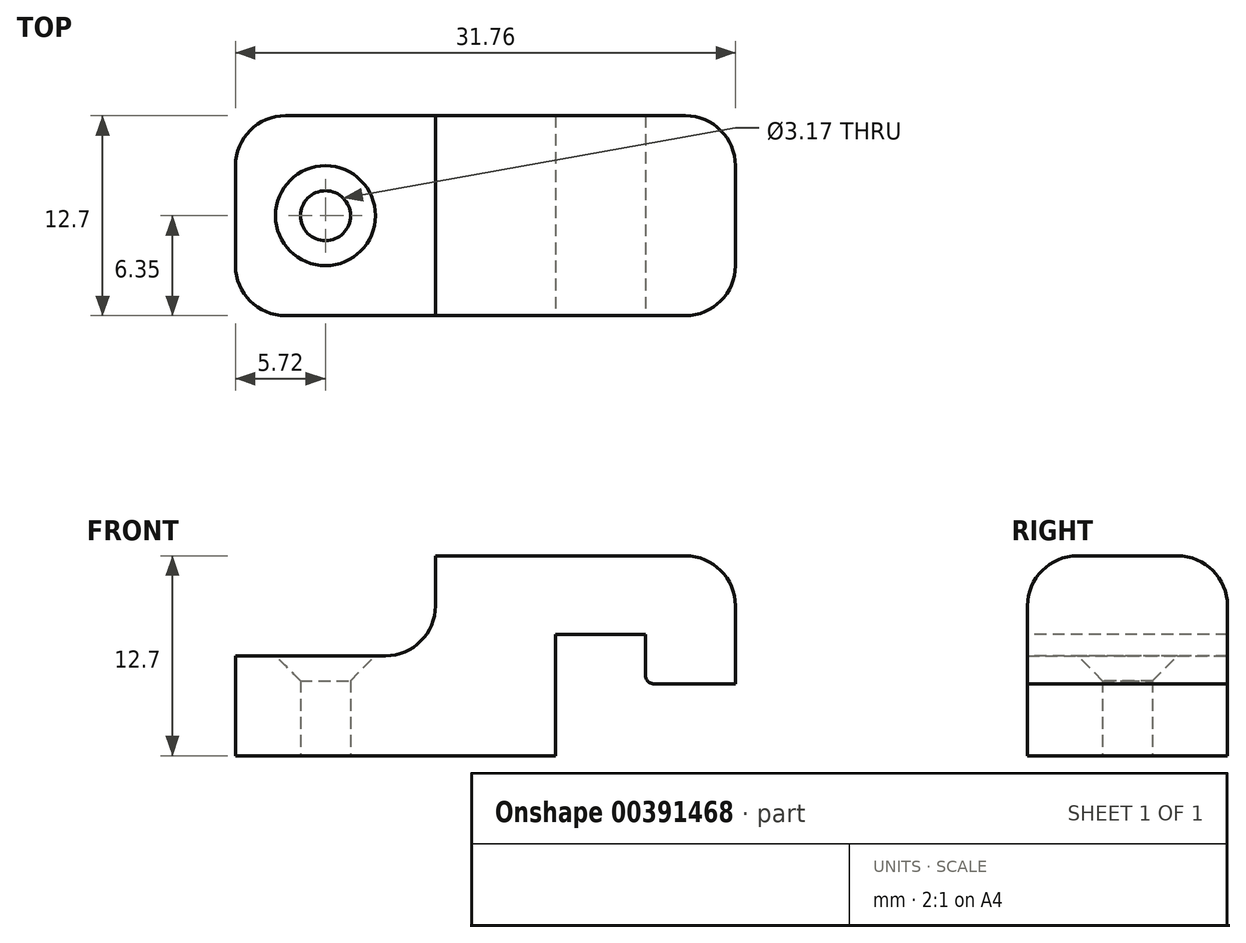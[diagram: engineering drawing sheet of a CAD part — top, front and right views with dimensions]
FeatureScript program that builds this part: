
annotation { "Feature Type Name" : "Feature", "Feature Type Description" : "" }
export const myFeature = defineFeature(function(context is Context, id is Id, definition is map)
    precondition{}
    {
        {
            var Q0;
            Q0=qCreatedBy(makeId("Top.planeOp"),FACE);
            var sketch = newSketch(context, id + "F0", { "sketchPlane" : qUnion([Q0])});
            skLineSegment(sketch, "E0.bottom", {"start": v(15.88, 6.35) * mm, "end": v(-15.88, 6.35) * mm});
            skLineSegment(sketch, "E0.top", {"start": v(15.88, -6.35) * mm, "end": v(-15.88, -6.35) * mm});
            skLineSegment(sketch, "E0.left", {"start": v(15.88, 6.35) * mm, "end": v(15.88, -6.35) * mm});
            skLineSegment(sketch, "E0.right", {"start": v(-15.88, 6.35) * mm, "end": v(-15.88, -6.35) * mm});
            skPoint(sketch, "E0.middle", {"position": v(0, 0) * mm});
            skCircle(sketch, "E1", {"center": v(-10.16, 0) * mm, "radius": 1.59 * mm});
            skSolve(sketch);
        }
        {
            var Q0;
            Q0 = qSketchRegion(id + "F0", true);
            extrude(context, id + "F1", {"entities" : qUnion([Q0]), "depth" : 12.7 * mm});
        }
        {
            var Q0;
            Q0=makeQuery(id+"F1.opExtrude","SWEPT_FACE",FACE,{"disambiguationData":[OSD([sQuery(id+"F0.wireOp",EDGE,"E0.top")])]});
            var sketch = newSketch(context, id + "F2", { "sketchPlane" : qUnion([Q0])});
            skLineSegment(sketch, "E2.bottom", {"start": v(15.88, 0) * mm, "end": v(4.44, 0) * mm});
            skLineSegment(sketch, "E2.top", {"start": v(15.88, 4.57) * mm, "end": v(10.7, 4.57) * mm});
            skLineSegment(sketch, "E2.left", {"start": v(15.88, 0) * mm, "end": v(15.88, 4.57) * mm});
            skLineSegment(sketch, "E2.right", {"start": v(4.44, 0) * mm, "end": v(4.44, 4.57) * mm});
            skLineSegment(sketch, "E3.top", {"start": v(4.44, 7.7) * mm, "end": v(10.16, 7.7) * mm});
            skLineSegment(sketch, "E3.left", {"start": v(4.44, 4.57) * mm, "end": v(4.44, 7.7) * mm});
            skLineSegment(sketch, "E3.right", {"start": v(10.16, 5.1) * mm, "end": v(10.16, 7.7) * mm});
            skPoint(sketch, "E4.visualSharp", {"position": v(10.16, 4.57) * mm});
            skArc(sketch, "E4.filletArc", {"start": v(10.16, 5.1) * mm, "mid": v(10.32, 4.73) * mm, "end": v(10.7, 4.57) * mm});
            skLineSegment(sketch, "E5.bottom", {"start": v(-15.88, 12.7) * mm, "end": v(-3.17, 12.7) * mm});
            skLineSegment(sketch, "E5.top", {"start": v(-15.88, 6.35) * mm, "end": v(-3.17, 6.35) * mm});
            skLineSegment(sketch, "E5.left", {"start": v(-15.88, 12.7) * mm, "end": v(-15.88, 6.35) * mm});
            skLineSegment(sketch, "E5.right", {"start": v(-3.17, 12.7) * mm, "end": v(-3.17, 6.35) * mm});
            skSolve(sketch);
        }
        {
            var Q0;
            Q0=makeQuery(id+"F1.opExtrude","CAP_EDGE",EDGE,{"disambiguationData":[OSD([sQuery(id+"F0.wireOp",EDGE,"E0.left")])],"isStart":false});
            var Q1;
            Q1=makeQuery(id+"F1.opExtrude","CAP_EDGE",EDGE,{"disambiguationData":[OSD([sQuery(id+"F0.wireOp",EDGE,"E0.top")])],"isStart":false});
            var Q2;
            Q2=makeQuery(id+"F1.opExtrude","CAP_EDGE",EDGE,{"disambiguationData":[OSD([sQuery(id+"F0.wireOp",EDGE,"E0.bottom")])],"isStart":false});
            var Q3;
            Q3=makeQuery(id+"F1.opExtrude","CAP_EDGE",EDGE,{"disambiguationData":[OSD([sQuery(id+"F0.wireOp",EDGE,"E0.right")])],"isStart":false});
            var Q4;
            Q4=makeQuery(id+"F1.opExtrude","SWEPT_EDGE",EDGE,{"disambiguationData":[OSD([sQuery(id+"F0.wireOp",EDGE,"E0.top"),sQuery(id+"F0.wireOp",EDGE,"E0.right")])]});
            var Q5;
            Q5=makeQuery(id+"F1.opExtrude","SWEPT_EDGE",EDGE,{"disambiguationData":[OSD([sQuery(id+"F0.wireOp",EDGE,"E0.top"),sQuery(id+"F0.wireOp",EDGE,"E0.left")])]});
            var Q6;
            Q6=makeQuery(id+"F1.opExtrude","SWEPT_EDGE",EDGE,{"disambiguationData":[OSD([sQuery(id+"F0.wireOp",EDGE,"E0.bottom"),sQuery(id+"F0.wireOp",EDGE,"E0.right")])]});
            var Q7;
            Q7=makeQuery(id+"F1.opExtrude","SWEPT_EDGE",EDGE,{"disambiguationData":[OSD([sQuery(id+"F0.wireOp",EDGE,"E0.bottom"),sQuery(id+"F0.wireOp",EDGE,"E0.left")])]});
            fillet(context, id + "F3", {"entities" : qUnion([Q0, Q1, Q2, Q3, Q4, Q5, Q6, Q7]), "radius" : 3.17 * mm, "tangentPropagation" : true, "allowEdgeOverflow" : false});
        }
        {
            var Q0;
            Q0 = qSketchRegion(id + "F2", true);
            extrude(context, id + "F4", {"entities" : qUnion([Q0]), "operationType" : NewBodyOperationType.REMOVE, "oppositeDirection" : true, "depth" : 12.7 * mm});
        }
        {
            var Q0;
            Q0=makeQuery(id+"F4.boolean.opBoolean","COPY",EDGE,{"derivedFrom":makeQuery(id+"F4.opExtrude","SWEPT_EDGE",EDGE,{"disambiguationData":[OSD([sQuery(id+"F0.wireOp",EDGE,"E0.top"),sQuery(id+"F2.wireOp",EDGE,"E5.bottom"),sQuery(id+"F2.wireOp",EDGE,"E5.right")])]})});
            var Q1;
            Q1=makeQuery(id+"F4.boolean.opBoolean","COPY",EDGE,{"derivedFrom":makeQuery(id+"F4.opExtrude","SWEPT_EDGE",EDGE,{"disambiguationData":[OSD([sQuery(id+"F2.wireOp",EDGE,"E5.top"),sQuery(id+"F2.wireOp",EDGE,"E5.right")])]})});
            fillet(context, id + "F5", {"entities" : qUnion([Q0, Q1]), "radius" : 3.17 * mm, "tangentPropagation" : true, "allowEdgeOverflow" : false});
        }
        {
            var Q0;
            Q0=makeQuery(id+"F4.boolean.opBoolean","INTERSECT",EDGE,{"derivedFrom":[makeQuery(id+"F1.opExtrude","SWEPT_FACE",FACE,{"disambiguationData":[OSD([sQuery(id+"F0.wireOp",EDGE,"E1")])]}),makeQuery(id+"F4.opExtrude","SWEPT_FACE",FACE,{"disambiguationData":[OSD([sQuery(id+"F2.wireOp",EDGE,"E5.top")])]})]});
            chamfer(context, id + "F6", {"entities" : qUnion([Q0]), "width" : 1.59 * mm, "tangentPropagation" : true});
        }
    });
